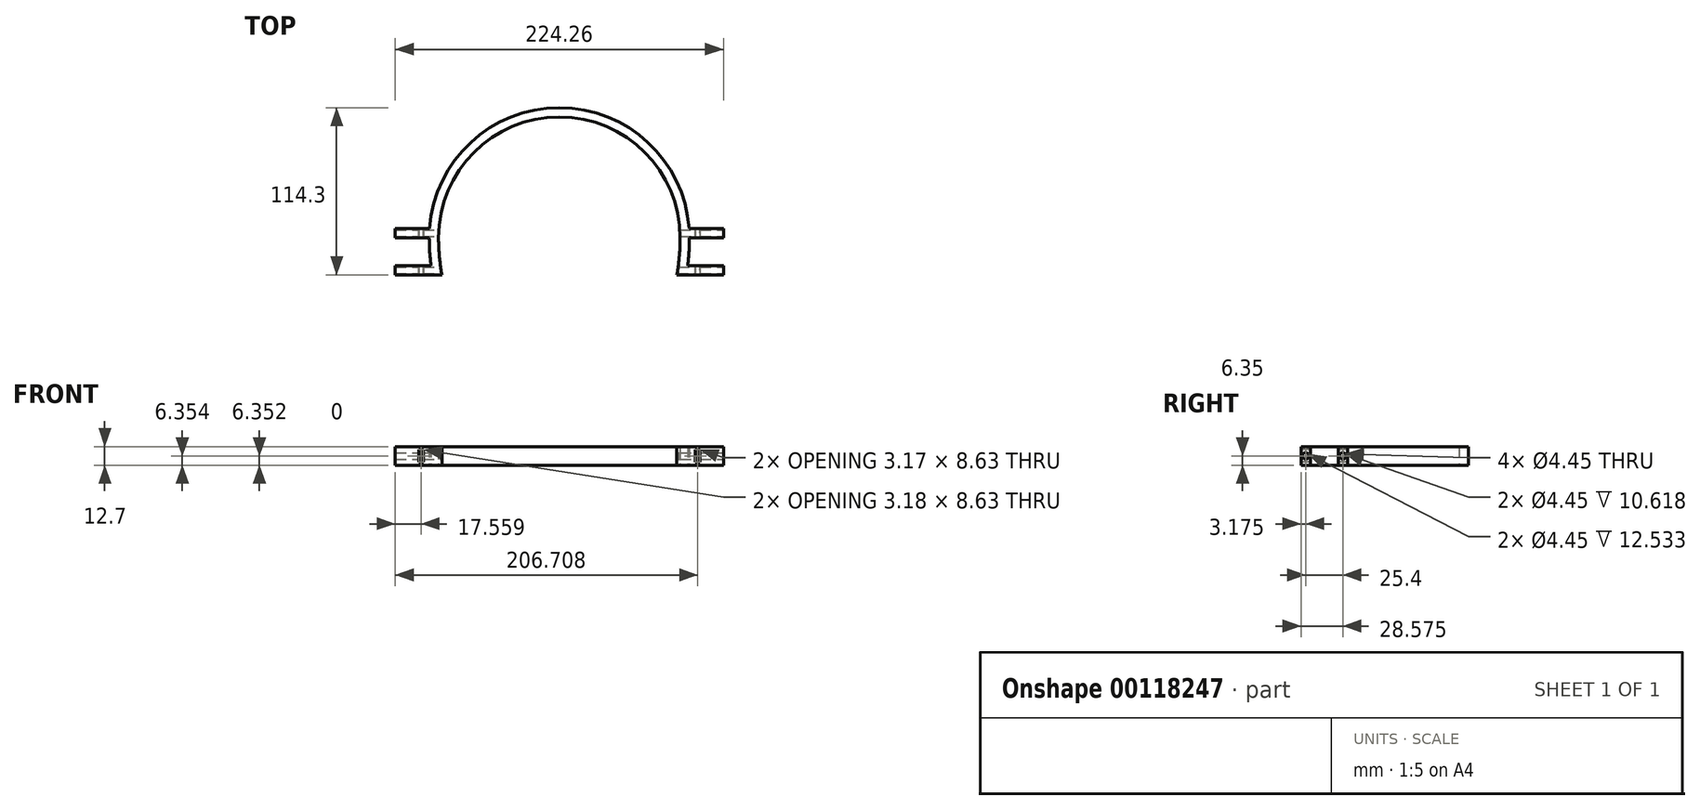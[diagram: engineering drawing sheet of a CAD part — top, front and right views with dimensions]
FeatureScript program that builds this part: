
annotation { "Feature Type Name" : "Feature", "Feature Type Description" : "" }
export const myFeature = defineFeature(function(context is Context, id is Id, definition is map)
    precondition{}
    {
        {
            var Q0;
            Q0=qCreatedBy(makeId("Top.planeOp"),FACE);
            var sketch = newSketch(context, id + "F0", { "sketchPlane" : qUnion([Q0])});
            skLineSegment(sketch, "E0", {"start": v(0, 0) * mm, "end": v(82.55, 0) * mm, "construction": true});
            skLineSegment(sketch, "E1", {"start": v(0, 0) * mm, "end": v(-82.55, 0) * mm, "construction": true});
            skLineSegment(sketch, "E2", {"start": v(0, 31.75) * mm, "end": v(-76.2, 31.75) * mm, "construction": true});
            skLineSegment(sketch, "E3", {"start": v(0, 31.75) * mm, "end": v(76.2, 31.75) * mm, "construction": true});
            skEllipticalArc(sketch, "E4", {});
            skLineSegment(sketch, "E5", {"start": v(-82.55, 0) * mm, "end": v(-88.9, 0) * mm, "construction": true});
            skLineSegment(sketch, "E6", {"start": v(82.55, 0) * mm, "end": v(88.9, 0) * mm, "construction": true});
            skLineSegment(sketch, "E7", {"start": v(0, 82.55) * mm, "end": v(0, 88.9) * mm, "construction": true});
            skEllipticalArc(sketch, "E8", {});
            skLineSegment(sketch, "E9", {"start": v(0, 82.55) * mm, "end": v(0, 0) * mm, "construction": true});
            skLineSegment(sketch, "E10", {"start": v(0, -69.85) * mm, "end": v(-63.5, -69.85) * mm, "construction": true});
            skLineSegment(sketch, "E11", {"start": v(0, -69.85) * mm, "end": v(63.5, -69.85) * mm, "construction": true});
            skEllipticalArc(sketch, "E12", {});
            skEllipticalArc(sketch, "E13", {});
            skPoint(sketch, "E14.end.orphan", {"position": v(0, -115.67) * mm});
            skPoint(sketch, "E15.end.orphan", {"position": v(0, -109.32) * mm});
            skLineSegment(sketch, "E16", {"start": v(-63.5, -69.85) * mm, "end": v(-70.86, -69.85) * mm});
            skEllipticalArc(sketch, "E17.trimOffspring", {});
            skEllipticalArc(sketch, "E18.trimOffspring", {});
            skLineSegment(sketch, "E19", {"start": v(0, 0) * mm, "end": v(0, -25.4) * mm});
            skLineSegment(sketch, "E20", {"start": v(-80.3, -25.4) * mm, "end": v(-86.73, -25.4) * mm});
            skLineSegment(sketch, "E21", {"start": v(80.3, -25.4) * mm, "end": v(86.73, -25.4) * mm});
            skLineSegment(sketch, "E22", {"start": v(-86.73, -25.4) * mm, "end": v(-112.13, -25.4) * mm});
            skLineSegment(sketch, "E23", {"start": v(86.73, -25.4) * mm, "end": v(112.13, -25.4) * mm});
            skLineSegment(sketch, "E24", {"start": v(-112.13, -25.4) * mm, "end": v(-112.13, -19.05) * mm});
            skLineSegment(sketch, "E25", {"start": v(112.13, -25.4) * mm, "end": v(112.13, -19.05) * mm});
            skLineSegment(sketch, "E26", {"start": v(-112.13, -19.05) * mm, "end": v(-87.69, -19.05) * mm});
            skLineSegment(sketch, "E27", {"start": v(112.13, -19.05) * mm, "end": v(87.69, -19.05) * mm});
            skLineSegment(sketch, "E28", {"start": v(-112.13, 0) * mm, "end": v(-88.9, 0) * mm});
            skLineSegment(sketch, "E29", {"start": v(-112.13, 0) * mm, "end": v(-112.13, 6.35) * mm});
            skLineSegment(sketch, "E30", {"start": v(112.13, 0) * mm, "end": v(112.13, 6.35) * mm});
            skLineSegment(sketch, "E31", {"start": v(-112.13, 6.35) * mm, "end": v(-88.67, 6.35) * mm});
            skLineSegment(sketch, "E32", {"start": v(112.13, 6.35) * mm, "end": v(88.67, 6.35) * mm});
            skLineSegment(sketch, "E33", {"start": v(112.13, 0) * mm, "end": v(88.9, 0) * mm});
            const initialGuessF0  = {"E4": [0, 0, -1, 0, 0.08255, 0.08255, 3.141592653589793, 0], "E8": [0, 0, -1, 0, 0.0889, 0.0889, 3.2130821034753123, 6.211695857294066], "E12": [0, 0, -1, 0, 0.08255, 0.10931637389453279, 6.283185307179586, 0.23449631493369694], "E13": [0, 0, -1, 0, 0.0889, 0.11566637389453278, 6.283185307179586, 0.165451643050746], "E17.trimOffspring": [0, 0, -1, 0, 0.08255, 0.10931637389453279, 2.907096338656096, 3.141592653589793], "E18.trimOffspring": [0, 0, -1, 0, 0.0889, 0.11566637389453278, 2.9761410105390462, 3.141592653589793]};
            skSetInitialGuess(sketch, initialGuessF0);
            skSolve(sketch);
        }
        {
            var Q0;
            Q0 = qSketchRegion(id + "F0", true);
            extrude(context, id + "F1", {"entities" : qUnion([Q0]), "depth" : 12.7 * mm});
        }
        {
            var Q0;
            Q0=makeQuery(id+"F1.opExtrude","SWEPT_FACE",FACE,{"disambiguationData":[OSD([sQuery(id+"F0.wireOp",EDGE,"E30")])]});
            var sketch = newSketch(context, id + "F2", { "sketchPlane" : qUnion([Q0])});
            skLineSegment(sketch, "E34", {"start": v(3.18, 12.7) * mm, "end": v(3.18, 0) * mm, "construction": true});
            skLineSegment(sketch, "E35", {"start": v(3.18, 6.35) * mm, "end": v(-22.23, 6.35) * mm, "construction": true});
            skPoint(sketch, "E35.endSnap0", {"position": v(3.18, 6.35) * mm});
            skCircle(sketch, "E36", {"center": v(-22.23, 6.35) * mm, "radius": 2.22 * mm});
            skCircle(sketch, "E37", {"center": v(3.18, 6.35) * mm, "radius": 2.22 * mm});
            skSolve(sketch);
        }
        {
            var Q0;
            Q0 = qSketchRegion(id + "F2", true);
            extrude(context, id + "F3", {"entities" : qUnion([Q0]), "operationType" : NewBodyOperationType.REMOVE, "endBound" : BoundingType.THROUGH_ALL, "oppositeDirection" : true, "depth" : 25.4 * mm});
        }
        {
            var Q0;
            Q0=makeQuery(id+"F1.opExtrude","SWEPT_FACE",FACE,{"disambiguationData":[OSD([sQuery(id+"F0.wireOp",EDGE,"E20"),sQuery(id+"F0.wireOp",EDGE,"E22")])]});
            var sketch = newSketch(context, id + "F4", { "sketchPlane" : qUnion([Q0])});
            skLineSegment(sketch, "E38", {"start": v(-80.3, 6.35) * mm, "end": v(-93, 6.35) * mm, "construction": true});
            skLineSegment(sketch, "E39", {"start": v(-93, 6.35) * mm, "end": v(-96.17, 6.35) * mm, "construction": true});
            skLineSegment(sketch, "E40", {"start": v(-93, 6.35) * mm, "end": v(-93, 10.67) * mm});
            skLineSegment(sketch, "E41", {"start": v(-93, 10.67) * mm, "end": v(-96.16, 10.67) * mm});
            skLineSegment(sketch, "E42", {"start": v(-96.16, 10.67) * mm, "end": v(-96.16, 2.04) * mm});
            skLineSegment(sketch, "E43", {"start": v(-96.16, 2.04) * mm, "end": v(-92.98, 2.04) * mm});
            skLineSegment(sketch, "E44", {"start": v(-92.98, 2.04) * mm, "end": v(-93, 6.35) * mm});
            skSolve(sketch);
        }
        {
            var Q0;
            Q0 = qSketchRegion(id + "F4", true);
            extrude(context, id + "F5", {"entities" : qUnion([Q0]), "operationType" : NewBodyOperationType.REMOVE, "endBound" : BoundingType.THROUGH_ALL, "oppositeDirection" : true, "depth" : 25.4 * mm});
        }
        {
            var Q0;
            Q0=makeQuery(id+"F1.opExtrude","SWEPT_FACE",FACE,{"disambiguationData":[OSD([sQuery(id+"F0.wireOp",EDGE,"E21"),sQuery(id+"F0.wireOp",EDGE,"E23")])]});
            var sketch = newSketch(context, id + "F6", { "sketchPlane" : qUnion([Q0])});
            skLineSegment(sketch, "E45", {"start": v(80.3, 6.35) * mm, "end": v(93, 6.35) * mm, "construction": true});
            skLineSegment(sketch, "E46", {"start": v(93, 6.35) * mm, "end": v(93, 10.67) * mm});
            skLineSegment(sketch, "E47", {"start": v(93, 10.67) * mm, "end": v(96.17, 10.67) * mm});
            skLineSegment(sketch, "E48", {"start": v(96.17, 10.67) * mm, "end": v(96.17, 2.04) * mm});
            skLineSegment(sketch, "E49", {"start": v(96.17, 2.04) * mm, "end": v(93, 2.04) * mm});
            skLineSegment(sketch, "E50", {"start": v(93, 2.04) * mm, "end": v(93, 6.35) * mm});
            skSolve(sketch);
        }
        {
            var Q0;
            Q0 = qSketchRegion(id + "F6", true);
            extrude(context, id + "F7", {"entities" : qUnion([Q0]), "operationType" : NewBodyOperationType.REMOVE, "endBound" : BoundingType.THROUGH_ALL, "oppositeDirection" : true, "depth" : 25.4 * mm});
        }
    });
